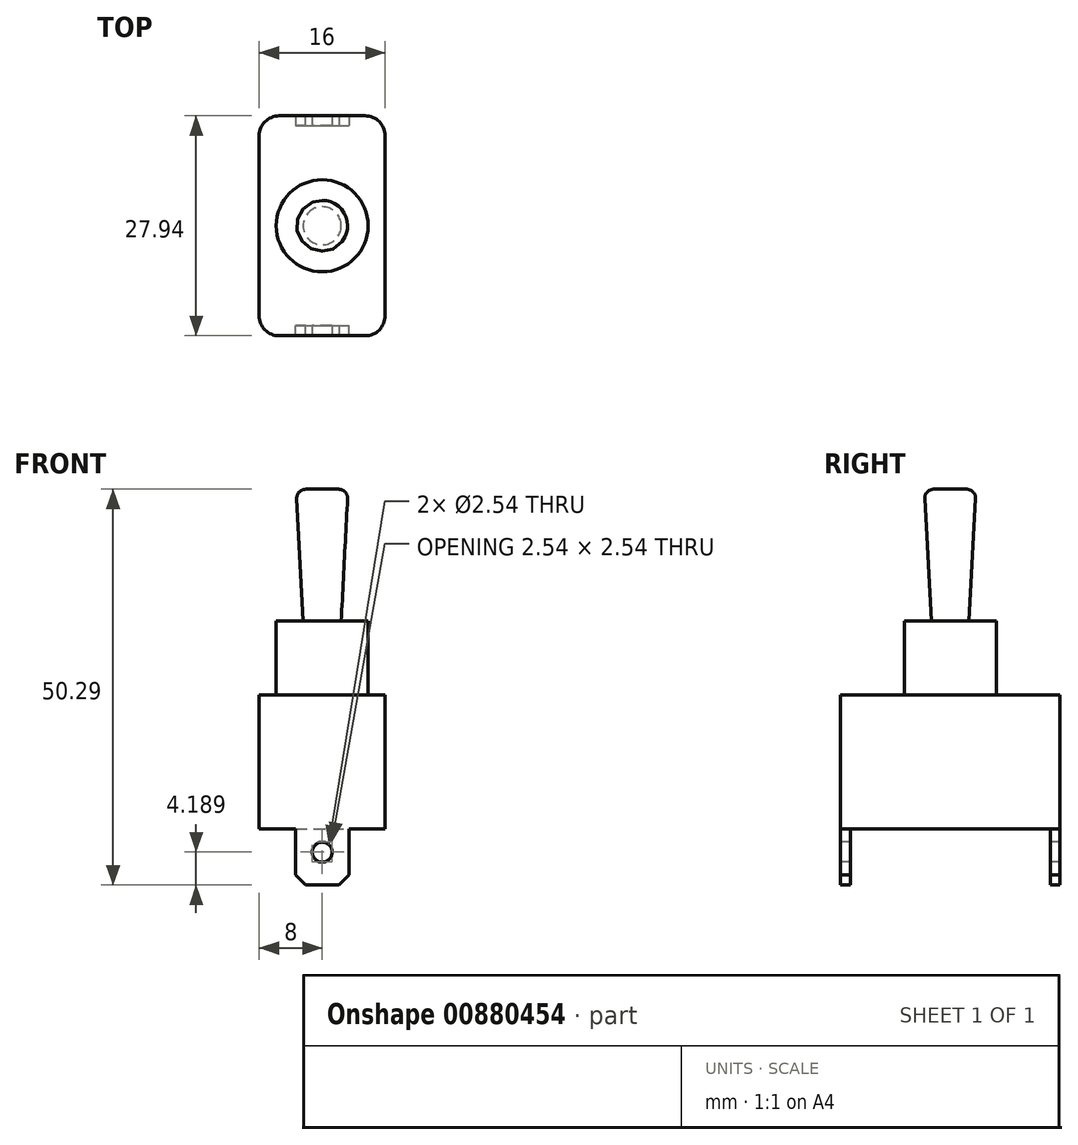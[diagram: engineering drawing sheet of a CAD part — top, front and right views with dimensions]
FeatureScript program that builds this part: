
annotation { "Feature Type Name" : "Feature", "Feature Type Description" : "" }
export const myFeature = defineFeature(function(context is Context, id is Id, definition is map)
    precondition{}
    {
        {
            var Q0;
            Q0=qCreatedBy(makeId("Top.planeOp"),FACE);
            var sketch = newSketch(context, id + "F0", { "sketchPlane" : qUnion([Q0])});
            skLineSegment(sketch, "E0.bottom", {"start": v(-5.46, -13.97) * mm, "end": v(5.46, -13.97) * mm});
            skLineSegment(sketch, "E0.top", {"start": v(-5.46, 13.97) * mm, "end": v(5.46, 13.97) * mm});
            skLineSegment(sketch, "E0.left", {"start": v(-8, -11.43) * mm, "end": v(-8, 11.43) * mm});
            skLineSegment(sketch, "E0.right", {"start": v(8, -11.43) * mm, "end": v(8, 11.43) * mm});
            skPoint(sketch, "E0.middle", {"position": v(0, 0) * mm});
            skPoint(sketch, "E1.visualSharp", {"position": v(-8, -13.97) * mm});
            skArc(sketch, "E1.filletArc", {"start": v(-8, -11.43) * mm, "mid": v(-7.26, -13.23) * mm, "end": v(-5.46, -13.97) * mm});
            skPoint(sketch, "E2.visualSharp", {"position": v(8, -13.97) * mm});
            skArc(sketch, "E2.filletArc", {"start": v(5.46, -13.97) * mm, "mid": v(7.26, -13.23) * mm, "end": v(8, -11.43) * mm});
            skPoint(sketch, "E3.visualSharp", {"position": v(-8, 13.97) * mm});
            skArc(sketch, "E3.filletArc", {"start": v(-5.46, 13.97) * mm, "mid": v(-7.26, 13.23) * mm, "end": v(-8, 11.43) * mm});
            skPoint(sketch, "E4.visualSharp", {"position": v(8, 13.97) * mm});
            skArc(sketch, "E4.filletArc", {"start": v(8, 11.43) * mm, "mid": v(7.26, 13.23) * mm, "end": v(5.46, 13.97) * mm});
            skSolve(sketch);
        }
        {
            var Q0;
            Q0 = qSketchRegion(id + "F0", true);
            extrude(context, id + "F1", {"entities" : qUnion([Q0]), "depth" : 17.02 * mm, "offsetDistance" : 25.4 * mm});
        }
        {
            var Q0;
            Q0=makeQuery(id+"F1.opExtrude","CAP_FACE",FACE,{"disambiguationData":[OSD([sQuery(id+"F0.wireOp",EDGE,"E0.bottom"),sQuery(id+"F0.wireOp",EDGE,"E0.top"),sQuery(id+"F0.wireOp",EDGE,"E0.left"),sQuery(id+"F0.wireOp",EDGE,"E0.right"),sQuery(id+"F0.wireOp",EDGE,"E1.filletArc"),sQuery(id+"F0.wireOp",EDGE,"E2.filletArc"),sQuery(id+"F0.wireOp",EDGE,"E3.filletArc"),sQuery(id+"F0.wireOp",EDGE,"E4.filletArc")])],"isStart":false});
            var sketch = newSketch(context, id + "F2", { "sketchPlane" : qUnion([Q0])});
            skCircle(sketch, "E5", {"center": v(0, 0) * mm, "radius": 5.84 * mm});
            skSolve(sketch);
        }
        {
            var Q0;
            Q0 = qSketchRegion(id + "F2", true);
            extrude(context, id + "F3", {"entities" : qUnion([Q0]), "operationType" : NewBodyOperationType.ADD, "depth" : 9.4 * mm, "offsetDistance" : 25.4 * mm});
        }
        {
            var Q0;
            Q0=makeQuery(id+"F3.opExtrude","CAP_FACE",FACE,{"disambiguationData":[OSD([sQuery(id+"F2.wireOp",EDGE,"E5")])],"isStart":false});
            var sketch = newSketch(context, id + "F4", { "sketchPlane" : qUnion([Q0])});
            skCircle(sketch, "E6", {"center": v(0, 0) * mm, "radius": 2.41 * mm});
            skSolve(sketch);
        }
        {
            var Q0;
            Q0 = qSketchRegion(id + "F4", true);
            extrude(context, id + "F5", {"entities" : qUnion([Q0]), "operationType" : NewBodyOperationType.ADD, "depth" : 16.76 * mm, "offsetDistance" : 25.4 * mm, "hasDraft" : true, "draftAngle" : 3 * degree});
        }
        {
            var Q0;
            Q0=makeQuery(id+"F5.opExtrude","CAP_EDGE",EDGE,{"disambiguationData":[OSD([sQuery(id+"F4.wireOp",EDGE,"E6")])],"isStart":false});
            fillet(context, id + "F6", {"entities" : qUnion([Q0]), "radius" : 1.12 * mm, "tangentPropagation" : true, "allowEdgeOverflow" : false});
        }
        {
            var Q0;
            Q0=makeQuery(id+"F1.opExtrude","CAP_FACE",FACE,{"disambiguationData":[OSD([sQuery(id+"F0.wireOp",EDGE,"E0.bottom"),sQuery(id+"F0.wireOp",EDGE,"E0.top"),sQuery(id+"F0.wireOp",EDGE,"E0.left"),sQuery(id+"F0.wireOp",EDGE,"E0.right"),sQuery(id+"F0.wireOp",EDGE,"E1.filletArc"),sQuery(id+"F0.wireOp",EDGE,"E2.filletArc"),sQuery(id+"F0.wireOp",EDGE,"E3.filletArc"),sQuery(id+"F0.wireOp",EDGE,"E4.filletArc")])],"isStart":true});
            var sketch = newSketch(context, id + "F7", { "sketchPlane" : qUnion([Q0])});
            skLineSegment(sketch, "E7.bottom", {"start": v(-3.4, -13.97) * mm, "end": v(3.4, -13.97) * mm});
            skLineSegment(sketch, "E7.top", {"start": v(-3.4, -12.7) * mm, "end": v(3.4, -12.7) * mm});
            skLineSegment(sketch, "E7.left", {"start": v(-3.4, -13.97) * mm, "end": v(-3.4, -12.7) * mm});
            skLineSegment(sketch, "E7.right", {"start": v(3.4, -13.97) * mm, "end": v(3.4, -12.7) * mm});
            skLineSegment(sketch, "E8.bottom", {"start": v(-3.4, 13.97) * mm, "end": v(3.4, 13.97) * mm});
            skLineSegment(sketch, "E8.top", {"start": v(-3.4, 12.7) * mm, "end": v(3.4, 12.7) * mm});
            skLineSegment(sketch, "E8.left", {"start": v(-3.4, 13.97) * mm, "end": v(-3.4, 12.7) * mm});
            skLineSegment(sketch, "E8.right", {"start": v(3.4, 13.97) * mm, "end": v(3.4, 12.7) * mm});
            skSolve(sketch);
        }
        {
            var Q0;
            Q0 = qSketchRegion(id + "F7", true);
            extrude(context, id + "F8", {"entities" : qUnion([Q0]), "operationType" : NewBodyOperationType.ADD, "depth" : 7.11 * mm, "offsetDistance" : 25.4 * mm});
        }
        {
            var Q0;
            Q0=makeQuery(id+"F8.opExtrude","CAP_EDGE",EDGE,{"disambiguationData":[OSD([sQuery(id+"F7.wireOp",EDGE,"E7.left")])],"isStart":false});
            var Q1;
            Q1=makeQuery(id+"F8.opExtrude","CAP_EDGE",EDGE,{"disambiguationData":[OSD([sQuery(id+"F7.wireOp",EDGE,"E7.right")])],"isStart":false});
            var Q2;
            Q2=makeQuery(id+"F8.opExtrude","CAP_EDGE",EDGE,{"disambiguationData":[OSD([sQuery(id+"F7.wireOp",EDGE,"E8.left")])],"isStart":false});
            var Q3;
            Q3=makeQuery(id+"F8.opExtrude","CAP_EDGE",EDGE,{"disambiguationData":[OSD([sQuery(id+"F7.wireOp",EDGE,"E8.right")])],"isStart":false});
            chamfer(context, id + "F9", {"entities" : qUnion([Q0, Q1, Q2, Q3]), "width" : 1.27 * mm, "tangentPropagation" : true});
        }
        {
            var Q0;
            Q0=makeQuery(id+"F8.boolean.opBoolean","MERGE",FACE,{"derivedFrom":[makeQuery(id+"F1.opExtrude","SWEPT_FACE",FACE,{"disambiguationData":[OSD([sQuery(id+"F0.wireOp",EDGE,"E0.top")])]}),makeQuery(id+"F8.opExtrude","SWEPT_FACE",FACE,{"disambiguationData":[OSD([sQuery(id+"F7.wireOp",EDGE,"E7.bottom")])]})]});
            var sketch = newSketch(context, id + "F10", { "sketchPlane" : qUnion([Q0])});
            skPoint(sketch, "E9", {"position": v(0, -2.92) * mm});
            skPoint(sketch, "E9.positionSnap0", {"position": v(0, -7.11) * mm});
            skPoint(sketch, "E9.positionSnap1", {"position": v(-3.4, -2.92) * mm});
            skSolve(sketch);
        }
        {
            var Q0;
            Q0=makeQuery(id+"F8.boolean.opBoolean","MERGE",FACE,{"derivedFrom":[makeQuery(id+"F1.opExtrude","SWEPT_FACE",FACE,{"disambiguationData":[OSD([sQuery(id+"F0.wireOp",EDGE,"E0.bottom")])]}),makeQuery(id+"F8.opExtrude","SWEPT_FACE",FACE,{"disambiguationData":[OSD([sQuery(id+"F7.wireOp",EDGE,"E8.bottom")])]})]});
            var sketch = newSketch(context, id + "F11", { "sketchPlane" : qUnion([Q0])});
            skPoint(sketch, "E10", {"position": v(0, -2.92) * mm});
            skPoint(sketch, "E10.positionSnap0", {"position": v(-3.4, -2.92) * mm});
            skPoint(sketch, "E10.positionSnap1", {"position": v(0, -7.11) * mm});
            skSolve(sketch);
        }
        {
            var Q0;
            Q0=sQuery(id+"F11.wireOp",VERTEX,"E10");
            var Q1;
            Q1=sQuery(id+"F10.wireOp",VERTEX,"E9");
            var Q2;
            Q2=makeQuery(id+"F1.opExtrude","SWEPT_BODY",BODY,{"disambiguationData":[OSD([sQuery(id+"F0.wireOp",EDGE,"E0.bottom"),sQuery(id+"F0.wireOp",EDGE,"E0.top"),sQuery(id+"F0.wireOp",EDGE,"E0.left"),sQuery(id+"F0.wireOp",EDGE,"E0.right"),sQuery(id+"F0.wireOp",EDGE,"E1.filletArc"),sQuery(id+"F0.wireOp",EDGE,"E2.filletArc"),sQuery(id+"F0.wireOp",EDGE,"E3.filletArc"),sQuery(id+"F0.wireOp",EDGE,"E4.filletArc")])]});
            hole(context, id + "F12", {"style" : HoleStyle.SIMPLE, "endStyle" : HoleEndStyle.THROUGH, "holeDiameter" : 2.54 * mm, "majorDiameter" : 6.35 * mm, "isTappedThrough" : true, "tappedDepth" : 12.7 * mm, "tapClearance" : 3, "locations" : qUnion([Q0, Q1]), "scope" : qUnion([Q2])});
        }
    });
